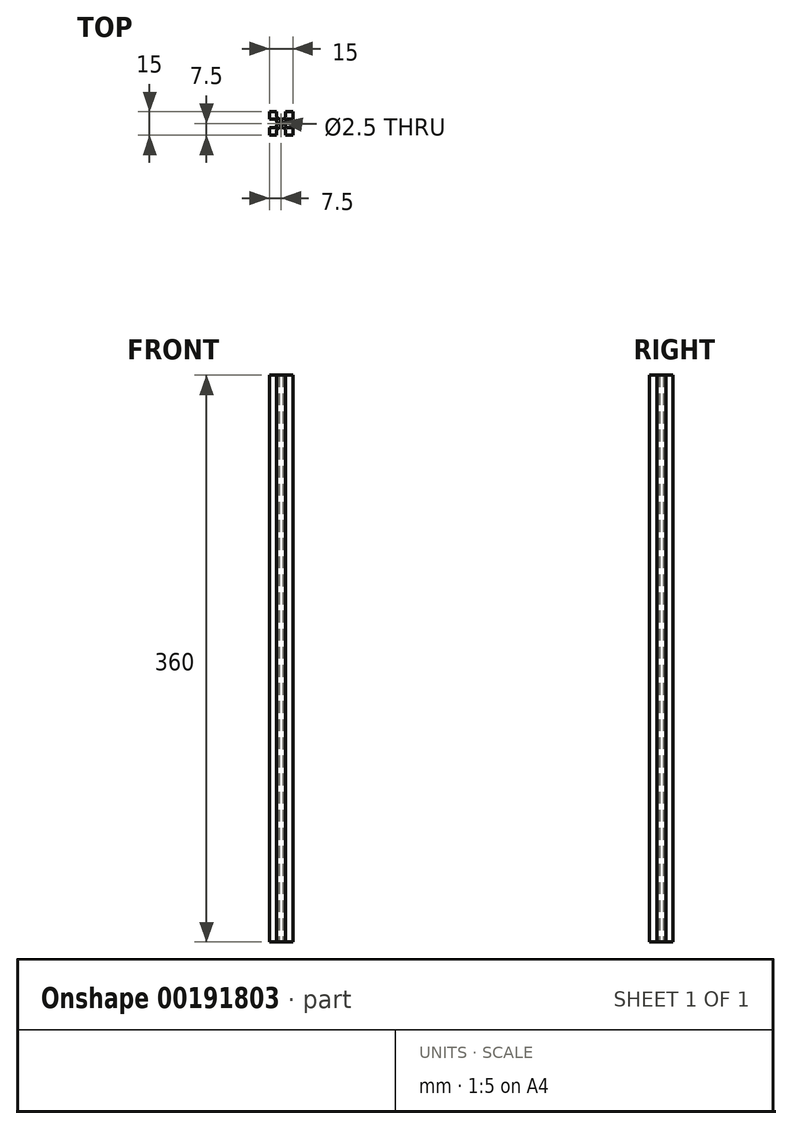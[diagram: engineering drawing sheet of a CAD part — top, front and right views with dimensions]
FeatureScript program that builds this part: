
annotation { "Feature Type Name" : "Feature", "Feature Type Description" : "" }
export const myFeature = defineFeature(function(context is Context, id is Id, definition is map)
    precondition{}
    {
        {
            var Q0;
            Q0=qCreatedBy(makeId("Top.planeOp"),FACE);
            var sketch = newSketch(context, id + "F0", { "sketchPlane" : qUnion([Q0])});
            skLineSegment(sketch, "E0.bottom", {"start": v(-7.5, 7.5) * mm, "end": v(7.5, 7.5) * mm});
            skLineSegment(sketch, "E0.top", {"start": v(-7.5, -7.5) * mm, "end": v(7.5, -7.5) * mm});
            skLineSegment(sketch, "E0.left", {"start": v(-7.5, 7.5) * mm, "end": v(-7.5, -7.5) * mm});
            skLineSegment(sketch, "E0.right", {"start": v(7.5, 7.5) * mm, "end": v(7.5, -7.5) * mm});
            skPoint(sketch, "E0.middle", {"position": v(0, 0) * mm});
            skLineSegment(sketch, "E1.bottom", {"start": v(-2.85, -7.5) * mm, "end": v(2.85, -7.5) * mm});
            skLineSegment(sketch, "E1.top", {"start": v(-0.85, -2.8) * mm, "end": v(0.85, -2.8) * mm});
            skLineSegment(sketch, "E1.left", {"start": v(-2.85, -7.5) * mm, "end": v(-2.85, -4.8) * mm});
            skLineSegment(sketch, "E1.right", {"start": v(2.85, -7.5) * mm, "end": v(2.85, -4.8) * mm});
            skLineSegment(sketch, "E2.bottom", {"start": v(7.5, -2.85) * mm, "end": v(4.8, -2.85) * mm});
            skLineSegment(sketch, "E2.top", {"start": v(7.5, 2.85) * mm, "end": v(4.8, 2.85) * mm});
            skLineSegment(sketch, "E2.left", {"start": v(7.5, -2.85) * mm, "end": v(7.5, 2.85) * mm});
            skLineSegment(sketch, "E2.right", {"start": v(2.8, -0.85) * mm, "end": v(2.8, 0.85) * mm});
            skLineSegment(sketch, "E3.bottom", {"start": v(2.85, 7.5) * mm, "end": v(-2.85, 7.5) * mm});
            skLineSegment(sketch, "E3.top", {"start": v(0.85, 2.8) * mm, "end": v(-0.85, 2.8) * mm});
            skLineSegment(sketch, "E3.left", {"start": v(2.85, 7.5) * mm, "end": v(2.85, 4.8) * mm});
            skLineSegment(sketch, "E3.right", {"start": v(-2.85, 7.5) * mm, "end": v(-2.85, 4.8) * mm});
            skLineSegment(sketch, "E4.bottom", {"start": v(-7.5, 2.85) * mm, "end": v(-4.8, 2.85) * mm});
            skLineSegment(sketch, "E4.top", {"start": v(-7.5, -2.85) * mm, "end": v(-4.8, -2.85) * mm});
            skLineSegment(sketch, "E4.left", {"start": v(-7.5, 2.85) * mm, "end": v(-7.5, -2.85) * mm});
            skLineSegment(sketch, "E4.right", {"start": v(-2.8, 0.85) * mm, "end": v(-2.8, -0.85) * mm});
            skCircle(sketch, "E5", {"center": v(0, 0) * mm, "radius": 1.25 * mm});
            skPoint(sketch, "E6.visualSharp", {"position": v(-2.85, -2.8) * mm});
            skArc(sketch, "E6.filletArc", {"start": v(-0.85, -2.8) * mm, "mid": v(-2.26, -3.39) * mm, "end": v(-2.85, -4.8) * mm});
            skPoint(sketch, "E7.visualSharp", {"position": v(2.85, -2.8) * mm});
            skArc(sketch, "E7.filletArc", {"start": v(2.85, -4.8) * mm, "mid": v(2.26, -3.39) * mm, "end": v(0.85, -2.8) * mm});
            skPoint(sketch, "E8.visualSharp", {"position": v(2.8, -2.85) * mm});
            skArc(sketch, "E8.filletArc", {"start": v(2.8, -0.85) * mm, "mid": v(3.39, -2.26) * mm, "end": v(4.8, -2.85) * mm});
            skPoint(sketch, "E9.visualSharp", {"position": v(2.8, 2.85) * mm});
            skArc(sketch, "E9.filletArc", {"start": v(4.8, 2.85) * mm, "mid": v(3.39, 2.26) * mm, "end": v(2.8, 0.85) * mm});
            skPoint(sketch, "E10.visualSharp", {"position": v(2.85, 2.8) * mm});
            skArc(sketch, "E10.filletArc", {"start": v(0.85, 2.8) * mm, "mid": v(2.26, 3.39) * mm, "end": v(2.85, 4.8) * mm});
            skPoint(sketch, "E11.visualSharp", {"position": v(-2.85, 2.8) * mm});
            skArc(sketch, "E11.filletArc", {"start": v(-2.85, 4.8) * mm, "mid": v(-2.26, 3.39) * mm, "end": v(-0.85, 2.8) * mm});
            skPoint(sketch, "E12.visualSharp", {"position": v(-2.8, 2.85) * mm});
            skArc(sketch, "E12.filletArc", {"start": v(-2.8, 0.85) * mm, "mid": v(-3.39, 2.26) * mm, "end": v(-4.8, 2.85) * mm});
            skPoint(sketch, "E13.visualSharp", {"position": v(-2.8, -2.85) * mm});
            skArc(sketch, "E13.filletArc", {"start": v(-4.8, -2.85) * mm, "mid": v(-3.39, -2.26) * mm, "end": v(-2.8, -0.85) * mm});
            skLineSegment(sketch, "E14.bottom", {"start": v(-2.85, -7.5) * mm, "end": v(-1.7, -7.5) * mm});
            skLineSegment(sketch, "E14.top", {"start": v(-2.85, -6.4) * mm, "end": v(-1.7, -6.4) * mm});
            skLineSegment(sketch, "E14.left", {"start": v(-2.85, -7.5) * mm, "end": v(-2.85, -6.4) * mm});
            skLineSegment(sketch, "E14.right", {"start": v(-1.7, -7.5) * mm, "end": v(-1.7, -6.4) * mm});
            skLineSegment(sketch, "E15.bottom", {"start": v(2.85, -7.5) * mm, "end": v(1.7, -7.5) * mm});
            skLineSegment(sketch, "E15.top", {"start": v(2.85, -6.4) * mm, "end": v(1.7, -6.4) * mm});
            skLineSegment(sketch, "E15.left", {"start": v(2.85, -7.5) * mm, "end": v(2.85, -6.4) * mm});
            skLineSegment(sketch, "E15.right", {"start": v(1.7, -7.5) * mm, "end": v(1.7, -6.4) * mm});
            skLineSegment(sketch, "E16.bottom", {"start": v(7.5, -2.85) * mm, "end": v(6.4, -2.85) * mm});
            skLineSegment(sketch, "E16.top", {"start": v(7.5, -1.7) * mm, "end": v(6.4, -1.7) * mm});
            skLineSegment(sketch, "E16.left", {"start": v(7.5, -2.85) * mm, "end": v(7.5, -1.7) * mm});
            skLineSegment(sketch, "E16.right", {"start": v(6.4, -2.85) * mm, "end": v(6.4, -1.7) * mm});
            skLineSegment(sketch, "E17.bottom", {"start": v(7.5, 2.85) * mm, "end": v(6.4, 2.85) * mm});
            skLineSegment(sketch, "E17.top", {"start": v(7.5, 1.7) * mm, "end": v(6.4, 1.7) * mm});
            skLineSegment(sketch, "E17.left", {"start": v(7.5, 2.85) * mm, "end": v(7.5, 1.7) * mm});
            skLineSegment(sketch, "E17.right", {"start": v(6.4, 2.85) * mm, "end": v(6.4, 1.7) * mm});
            skLineSegment(sketch, "E18.bottom", {"start": v(2.85, 7.5) * mm, "end": v(1.7, 7.5) * mm});
            skLineSegment(sketch, "E18.top", {"start": v(2.85, 6.4) * mm, "end": v(1.7, 6.4) * mm});
            skLineSegment(sketch, "E18.left", {"start": v(2.85, 7.5) * mm, "end": v(2.85, 6.4) * mm});
            skLineSegment(sketch, "E18.right", {"start": v(1.7, 7.5) * mm, "end": v(1.7, 6.4) * mm});
            skLineSegment(sketch, "E19.bottom", {"start": v(-2.85, 7.5) * mm, "end": v(-1.7, 7.5) * mm});
            skLineSegment(sketch, "E19.top", {"start": v(-2.85, 6.4) * mm, "end": v(-1.7, 6.4) * mm});
            skLineSegment(sketch, "E19.left", {"start": v(-2.85, 7.5) * mm, "end": v(-2.85, 6.4) * mm});
            skLineSegment(sketch, "E19.right", {"start": v(-1.7, 7.5) * mm, "end": v(-1.7, 6.4) * mm});
            skLineSegment(sketch, "E20.bottom", {"start": v(-7.5, 2.85) * mm, "end": v(-6.4, 2.85) * mm});
            skLineSegment(sketch, "E20.top", {"start": v(-7.5, 1.7) * mm, "end": v(-6.4, 1.7) * mm});
            skLineSegment(sketch, "E20.left", {"start": v(-7.5, 2.85) * mm, "end": v(-7.5, 1.7) * mm});
            skLineSegment(sketch, "E20.right", {"start": v(-6.4, 2.85) * mm, "end": v(-6.4, 1.7) * mm});
            skLineSegment(sketch, "E21.bottom", {"start": v(-7.5, -2.85) * mm, "end": v(-6.4, -2.85) * mm});
            skLineSegment(sketch, "E21.top", {"start": v(-7.5, -1.7) * mm, "end": v(-6.4, -1.7) * mm});
            skLineSegment(sketch, "E21.left", {"start": v(-7.5, -2.85) * mm, "end": v(-7.5, -1.7) * mm});
            skLineSegment(sketch, "E21.right", {"start": v(-6.4, -2.85) * mm, "end": v(-6.4, -1.7) * mm});
            skSolve(sketch);
        }
        {
            var Q0;
            Q0=makeQuery(id+"F0.imprint","IMPRINT",FACE,{"disambiguationData":[TD([[makeQuery(id+"F0.imprint","IMPRINT",EDGE,{"derivedFrom":sQuery(id+"F0.wireOp",EDGE,"E1.top")}),1.0]])]});
            var Q1;
            Q1=makeQuery(id+"F0.imprint","IMPRINT",FACE,{"disambiguationData":[TD([[makeQuery(id+"F0.imprint","IMPRINT",EDGE,{"derivedFrom":sQuery(id+"F0.wireOp",EDGE,"E20.bottom")}),-1.0]])]});
            var Q2;
            Q2=makeQuery(id+"F0.imprint","IMPRINT",FACE,{"disambiguationData":[TD([[makeQuery(id+"F0.imprint","IMPRINT",EDGE,{"derivedFrom":sQuery(id+"F0.wireOp",EDGE,"E21.bottom")}),1.0]])]});
            var Q3;
            Q3=makeQuery(id+"F0.imprint","IMPRINT",FACE,{"disambiguationData":[TD([[makeQuery(id+"F0.imprint","IMPRINT",EDGE,{"derivedFrom":sQuery(id+"F0.wireOp",EDGE,"E19.bottom")}),-1.0]])]});
            var Q4;
            Q4=makeQuery(id+"F0.imprint","IMPRINT",FACE,{"disambiguationData":[TD([[makeQuery(id+"F0.imprint","IMPRINT",EDGE,{"derivedFrom":sQuery(id+"F0.wireOp",EDGE,"E18.bottom")}),1.0]])]});
            var Q5;
            Q5=makeQuery(id+"F0.imprint","IMPRINT",FACE,{"disambiguationData":[TD([[makeQuery(id+"F0.imprint","IMPRINT",EDGE,{"derivedFrom":sQuery(id+"F0.wireOp",EDGE,"E17.bottom")}),1.0]])]});
            var Q6;
            Q6=makeQuery(id+"F0.imprint","IMPRINT",FACE,{"disambiguationData":[TD([[makeQuery(id+"F0.imprint","IMPRINT",EDGE,{"derivedFrom":sQuery(id+"F0.wireOp",EDGE,"E16.bottom")}),-1.0]])]});
            var Q7;
            Q7=makeQuery(id+"F0.imprint","IMPRINT",FACE,{"disambiguationData":[TD([[makeQuery(id+"F0.imprint","IMPRINT",EDGE,{"derivedFrom":sQuery(id+"F0.wireOp",EDGE,"E14.bottom")}),1.0]])]});
            var Q8;
            Q8=makeQuery(id+"F0.imprint","IMPRINT",FACE,{"disambiguationData":[TD([[makeQuery(id+"F0.imprint","IMPRINT",EDGE,{"derivedFrom":sQuery(id+"F0.wireOp",EDGE,"E15.bottom")}),-1.0]])]});
            extrude(context, id + "F1", {"entities" : qUnion([Q0, Q1, Q2, Q3, Q4, Q5, Q6, Q7, Q8]), "depth" : 360 * mm});
        }
    });
